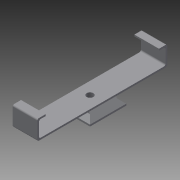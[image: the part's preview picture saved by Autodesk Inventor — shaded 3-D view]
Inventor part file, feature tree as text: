
AUTODESK INVENTOR PART (.ipt)
format: ipt  version: 2015 (Build 190159000, 159)  size: 150,528 bytes
history: native  units: mm
features: extrude x5, sketch x5, fillet x2, chamfer x1
ambient origin geometry x8: Origin, YZ Plane, XZ Plane, XY Plane, X Axis, Y Axis, Z Axis, Center Point
bodies: Solid1 (feature_tree)
feature tree (13):
  extrude  "Extrusion1"  Depth=43.5mm
  chamfer  "Chamfer1"  Distance=9.0mm
  extrude  "Extrusion2"  Depth=2.0mm TaperAngle=0.0deg
  extrude  "Extrusion3"  Depth=2.0mm
  fillet  "Fillet1"  Radius=8.0mm
  fillet  "Fillet2"  Radius=156.0mm
  extrude  "Extrusion4"  Depth=19.5mm
  extrude  "Extrusion5"  Depth=9.0mm
  sketch  "Sketch1"  dims[d0=43.5mm d1=43.5mm d2=9.0mm d3=0.0mm]
  sketch  "Sketch2"  dims[d4=7.0mm d5=2.0mm d6=45.0deg d7=2.0mm d8=0.0mm]
  sketch  "Sketch3"  dims[d15=10.0mm d16=2.0mm d17=8.0mm d21=156.0mm]
  sketch  "Sketch4"  dims[d22=23.5mm d23=19.5mm]
  sketch  "Sketch5"  dims[d24=2.0mm d27=9.0mm d28=63.25mm d29=29.5mm d30=0.0mm d31=1.0mm d32=2.0mm d33=13.25mm d34=8.0mm d35=0.0mm d36=8.0mm d37=44.75mm d38=0.0mm]
